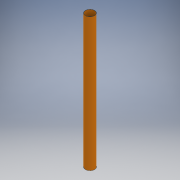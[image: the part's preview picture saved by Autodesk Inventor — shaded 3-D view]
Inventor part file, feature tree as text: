
AUTODESK INVENTOR PART (.ipt)
format: ipt  version: 2018 (Build 220112000, 112)  size: 96,768 bytes
history: native  units: mm
features: extrude x1, sketch x1
ambient origin geometry x8: Origin, YZ Plane, XZ Plane, XY Plane, X Axis, Y Axis, Z Axis, Center Point
bodies: Solido1 (feature_tree)
feature tree (2):
  extrude  "Estrusione1"  Depth=104.0mm
  sketch  "Schizzo1"
